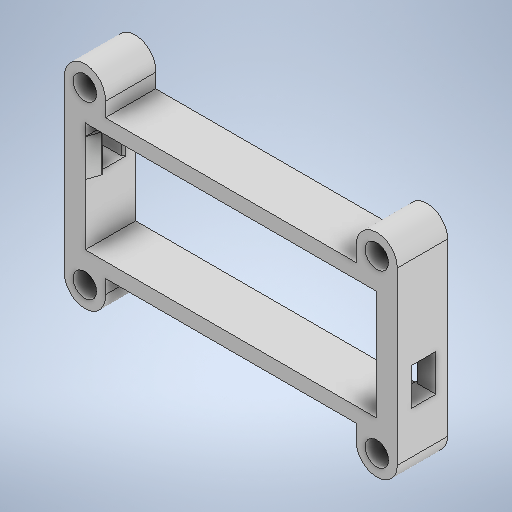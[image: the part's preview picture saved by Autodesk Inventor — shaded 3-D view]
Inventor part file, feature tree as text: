
AUTODESK INVENTOR PART (.ipt)
format: ipt  version: 2025.1 (Build 291241000, 241)  size: 347,648 bytes
history: native  units: mm
features: extrude x6, sketch x6, chamfer x4, plane x1
ambient origin geometry x8: Origin, YZ Plane, XZ Plane, XY Plane, X Axis, Y Axis, Z Axis, Center Point
bodies: Solid1 (feature_tree)
feature tree (17):
  extrude  "Extrusion1"  Depth=26.2mm
  sketch  "Sketch2"  dims[d2=3.5mm d3=3.5mm]
  sketch  "Sketch3"  dims[d4=69.5mm d5=12.0mm d6=0.0mm]
  extrude  "Extrusion2"  Depth=3.5mm
  extrude  "Extrusion3"  Depth=12.0mm TaperAngle=0.0deg
  extrude  "Extrusion4"  Depth=2.8mm
  extrude  "Extrusion5"  Depth=8.85mm
  chamfer  "Chamfer1"  Distance=2.8mm
  extrude  "Extrusion6"  Depth=5.8mm
  chamfer  "Chamfer2"  Distance=8.85mm
  chamfer  "Chamfer3"  Distance=12.0mm
  chamfer  "Chamfer4"  Distance=10.0mm
  plane  "Work Plane1"
  sketch  "Sketch1"  dims[d0=5.0mm d1=26.2mm]
  sketch  "Sketch4"  dims[d7=2.8mm d8=2.8mm]
  sketch  "Sketch5"  dims[d9=5.8mm d10=8.85mm]
  sketch  "Sketch6"  dims[d11=2.8mm d12=2.8mm d13=5.8mm d14=8.85mm d15=12.0mm d16=0.0mm d17=10.0mm d18=0.0mm d19=4.9mm d20=5.6mm d21=3.8mm d22=10.0mm d23=0.0mm d24=1.2mm d25=0.0mm d26=3.4mm d27=1.2mm d28=45.0deg d29=1.2mm d30=0.0mm d31=3.4mm d32=1.2mm d33=45.0deg d34=0.5mm d35=1.2mm d36=45.0deg d37=0.5mm d38=1.2mm d39=45.0deg]
